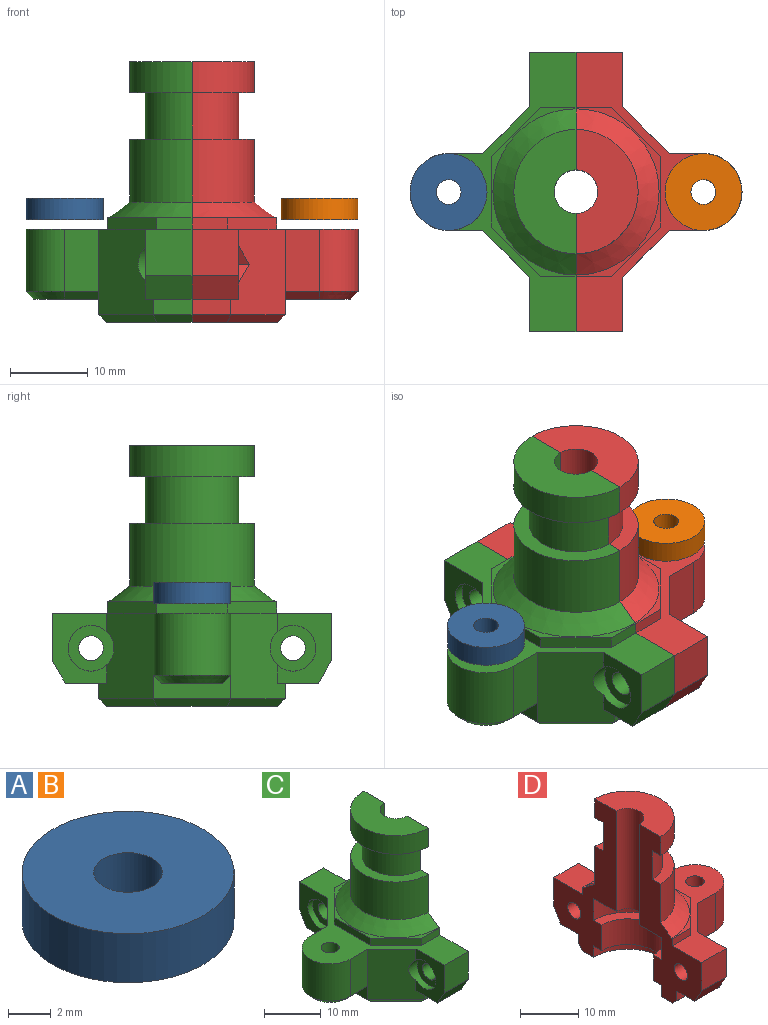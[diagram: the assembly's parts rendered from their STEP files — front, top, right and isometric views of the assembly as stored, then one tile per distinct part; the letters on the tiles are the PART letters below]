
ASSEMBLY  parts=4 mates=1
PART A: 4 faces, bbox 9.9x9.9x2.8 mm
  f0: plane 9.9x9.9mm, normal (0,0,1), area 68.9mm2, adj f2,f3
  f1: plane 9.9x9.9mm, normal (0,0,-1), area 68.9mm2, adj f2,f3
  f2: cylinder r=4.95mm len=9.9mm, axis (0,0,-1), area 87.1mm2, adj f0,f1
  f3: cylinder r=1.6mm len=3.2mm, axis (0,0,-1), area 28.1mm2, adj f0,f1
PART B: same geometry as A
PART C: 58 faces, bbox 21.4x36x33.6 mm
  f0: plane 9x7.03mm, normal (-1,0,0), area 36mm2, adj f12,f13,f15,f19,f32,f49
  f1: plane 6x5.33mm, normal (0,0,-1), area 26.3mm2, adj f16,f20,f36,f37,f40
  f2: cylinder r=8mm len=16mm, axis (0,0,-1), area 203.6mm2, adj f8,f11,f39,f40
  f3: plane 4.52x1.5mm, normal (0,1,0), area 6.8mm2, adj f5,f12,f29,f40
  f4: plane 4.52x1.5mm, normal (0,-1,0), area 6.8mm2, adj f5,f12,f31,f39
  f5: plane 21.8x10.9mm, normal (0,0,1), area 17mm2, adj f3,f4,f11,f29,f30,f31,f39,f40
  f6: cylinder r=6mm len=12mm, axis (0,0,-1), area 113.1mm2, adj f7,f8,f39,f40
  f7: plane 16x8mm, normal (0,0,-1), area 44mm2, adj f6,f10,f39,f40
  f8: plane 16x8mm, normal (0,0,1), area 44mm2, adj f2,f6,f39,f40
  f9: plane 16x8mm, normal (0,0,1), area 88.2mm2, adj f10,f27,f39,f40
  f10: cylinder r=8mm len=16mm, axis (0,0,-1), area 100.5mm2, adj f7,f9,f39,f40
  f11: cone r=8mm half-angle=53.5deg, axis (0,0,-1), area 98.7mm2, adj f2,f5,f39,f40
  f12: plane 36x21.37mm, normal (0,0,1), area 189.3mm2, adj f0,f3,f4,f13,f14,f29,f30,f31
  f13: plane 6x6mm, normal (0,-1,0), area 36mm2, adj f0,f12,f19,f39
  f14: plane 6.06x6mm, normal (0,1,0), area 36.3mm2, adj f12,f20,f37,f40
  f15: plane 6x5.3mm, normal (0,0,-1), area 26.1mm2, adj f0,f18,f19,f32,f39
  f16: plane 4.97x2mm, normal (0,1,0), area 9.9mm2, adj f1,f36,f40,f57
  f17: plane 22x11mm, normal (0,0,-1), area 92.3mm2, adj f21,f39,f40,f53,f54,f55,f56,f57
  f18: plane 4.97x2mm, normal (0,-1,0), area 9.9mm2, adj f15,f32,f39,f53
  f19: plane 6x3mm, normal (0,-0.87,-0.5), area 20.8mm2, adj f0,f13,f15,f39
  f20: plane 6x2.94mm, normal (0,0.87,-0.5), area 20.4mm2, adj f1,f14,f37,f40
  f21: cylinder r=8.3mm len=16.6mm, axis (0,0,-1), area 62.6mm2, adj f17,f25,f39,f40
  f22: plane 16.6x8.3mm, normal (0,0,-1), area 95.9mm2, adj f26,f27,f39,f40
  f23: cylinder r=6.3mm len=12.6mm, axis (0,0,-1), area 106.9mm2, adj f24,f25,f39,f40
  f24: plane 16.6x8.3mm, normal (0,0,1), area 45.9mm2, adj f23,f26,f39,f40
  f25: plane 16.6x8.3mm, normal (0,0,-1), area 45.9mm2, adj f21,f23,f39,f40
  f26: cylinder r=8.3mm len=16.6mm, axis (0,0,-1), area 119.9mm2, adj f22,f24,f39,f40
  f27: cylinder r=2.8mm len=21.2mm, axis (0,0,1), area 186.5mm2, adj f9,f22,f39,f40
  f28: plane 8.37x7.94mm, normal (0,0,-1), area 32.4mm2, adj f38,f43,f50,f51,f52
  f29: plane 6.39x6.39mm, normal (-0.71,0.71,0), area 13.5mm2, adj f3,f5,f12,f30
  f30: plane 9.03x1.5mm, normal (-1,0,0), area 13.5mm2, adj f5,f12,f29,f31
  f31: plane 6.39x6.39mm, normal (-0.71,-0.71,0), area 13.5mm2, adj f4,f5,f12,f30
  f32: plane 11x7.03mm, normal (-0.71,-0.71,0), area 92.4mm2, adj f0,f12,f15,f18,f33,f38,f49,f54
  f33: plane 8x4.4mm, normal (0,-1,0), area 35.2mm2, adj f12,f32,f34,f52
  f34: cylinder r=4.97mm len=9.94mm, axis (0,0,1), area 124.9mm2, adj f12,f33,f35,f51
  f35: plane 8x4.4mm, normal (0,1,0), area 35.2mm2, adj f12,f34,f36,f50
  f36: plane 11x7.03mm, normal (-0.71,0.71,0), area 92.4mm2, adj f1,f12,f16,f35,f37,f38,f46,f56
  f37: plane 9x7.03mm, normal (-1,0,0), area 36.1mm2, adj f1,f12,f14,f20,f36,f46
  f38: plane 9.94x3mm, normal (-1,0,0), area 20.9mm2, adj f28,f32,f36,f50,f52,f55
  f39: plane 33.6x15.2mm, normal (1,0,0), area 203.2mm2, adj f2,f4,f5,f6,f7,f8,f9,f10
  f40: plane 33.6x15.2mm, normal (1,0,0), area 203.3mm2, adj f1,f2,f3,f5,f6,f7,f8,f9
  f41: cylinder r=1.6mm len=7.8mm, axis (0,0,-1), area 78.4mm2, adj f12,f42
  f42: plane 5.9x5.9mm, normal (0,0,-1), area 19.3mm2, adj f41,f43
  f43: cylinder r=2.95mm len=5.9mm, axis (0,0,-1), area 22.2mm2, adj f28,f42
  f44: cylinder r=1.6mm len=4.8mm, axis (-1,0,0), area 48.3mm2, adj f40,f45
  f45: plane 5.9x5.9mm, normal (-1,0,0), area 19.3mm2, adj f44,f46
  f46: cylinder r=2.95mm len=5.9mm, axis (-1,0,0), area 25.2mm2, adj f36,f37,f45
  f47: cylinder r=1.6mm len=4.8mm, axis (-1,0,0), area 48.3mm2, adj f39,f48
  f48: plane 5.9x5.9mm, normal (-1,0,0), area 19.3mm2, adj f47,f49
  f49: cylinder r=2.95mm len=5.9mm, axis (-1,0,0), area 25.2mm2, adj f0,f32,f48
  f50: plane 4.4x1mm, normal (0,0.71,-0.71), area 6.2mm2, adj f28,f35,f38,f51
  f51: cone r=3.97mm half-angle=45deg, axis (0,0,1), area 19.9mm2, adj f28,f34,f50,f52
  f52: plane 4.4x1mm, normal (0,-0.71,-0.71), area 6.2mm2, adj f28,f33,f38,f51
  f53: plane 4.97x1mm, normal (0,-0.71,-0.71), area 6.7mm2, adj f17,f18,f39,f54
  f54: plane 7.44x7.44mm, normal (-0.5,-0.5,-0.71), area 13.5mm2, adj f17,f32,f53,f55
  f55: plane 9.94x1mm, normal (-0.71,0,-0.71), area 13.5mm2, adj f17,f38,f54,f56
  f56: plane 7.44x7.44mm, normal (-0.5,0.5,-0.71), area 13.5mm2, adj f17,f36,f55,f57
  f57: plane 4.97x1mm, normal (0,0.71,-0.71), area 6.7mm2, adj f16,f17,f40,f56
PART D: 68 faces, bbox 21.4x36x33.6 mm
  f0: plane 11x7.03mm, normal (0.71,-0.71,0), area 91.6mm2, adj f1,f10,f11,f27,f30,f32,f48,f49
  f1: plane 9x7.03mm, normal (1,0,0), area 33.8mm2, adj f0,f19,f30,f31,f32,f47,f48,f49
  f2: cylinder r=1.6mm len=4mm, axis (-1,0,0), area 40.2mm2, adj f42,f53
  f3: cylinder r=1.6mm len=4mm, axis (-1,0,0), area 40.2mm2, adj f41,f46
  f4: plane 8.37x7.94mm, normal (0,0,-1), area 32.4mm2, adj f11,f45,f60,f61,f62
  f5: plane 6.39x6.39mm, normal (0.71,-0.71,0), area 13.5mm2, adj f6,f15,f32,f37
  f6: plane 9.03x1.5mm, normal (1,0,0), area 13.5mm2, adj f5,f7,f15,f32
  f7: plane 6.39x6.39mm, normal (0.71,0.71,0), area 13.5mm2, adj f6,f15,f32,f38
  f8: plane 8x4.4mm, normal (0,1,0), area 35.2mm2, adj f9,f12,f32,f60
  f9: cylinder r=4.97mm len=9.94mm, axis (0,0,1), area 124.9mm2, adj f8,f10,f32,f61
  f10: plane 8x4.4mm, normal (0,-1,0), area 35.2mm2, adj f0,f9,f32,f62
  f11: plane 9.94x3mm, normal (1,0,0), area 20.9mm2, adj f0,f4,f12,f60,f62,f65
  f12: plane 11x7.03mm, normal (0.71,0.71,0), area 91.6mm2, adj f8,f11,f13,f29,f32,f40,f54,f59
  f13: plane 9x7.03mm, normal (1,0,0), area 33.9mm2, adj f12,f17,f18,f32,f40,f54,f55,f56
  f14: cone r=8mm half-angle=53.5deg, axis (0,0,-1), area 98.7mm2, adj f15,f39,f41,f42
  f15: plane 21.8x10.9mm, normal (0,0,1), area 17mm2, adj f5,f6,f7,f14,f37,f38,f41,f42
  f16: plane 16x8mm, normal (0,0,1), area 44mm2, adj f36,f39,f41,f42
  f17: plane 6x2.94mm, normal (0,0.87,-0.5), area 20.4mm2, adj f13,f18,f40,f42
  f18: plane 6.06x6mm, normal (0,1,0), area 36.3mm2, adj f13,f17,f32,f42
  f19: plane 6x3mm, normal (0,-0.87,-0.5), area 20.8mm2, adj f1,f30,f31,f41
  f20: cylinder r=2.8mm len=21.2mm, axis (0,0,1), area 186.5mm2, adj f25,f34,f41,f42
  f21: plane 16.6x8.3mm, normal (0,0,-1), area 45.9mm2, adj f24,f26,f41,f42
  f22: cylinder r=8.3mm len=16.6mm, axis (0,0,-1), area 119.9mm2, adj f23,f25,f41,f42
  f23: plane 16.6x8.3mm, normal (0,0,1), area 45.9mm2, adj f22,f24,f41,f42
  f24: cylinder r=6.3mm len=12.6mm, axis (0,0,-1), area 106.9mm2, adj f21,f23,f41,f42
  f25: plane 16.6x8.3mm, normal (0,0,-1), area 95.9mm2, adj f20,f22,f41,f42
  f26: cylinder r=8.3mm len=16.6mm, axis (0,0,-1), area 62.6mm2, adj f21,f28,f41,f42
  f27: plane 4.97x2mm, normal (0,-1,0), area 9.9mm2, adj f0,f30,f41,f63
  f28: plane 22x11mm, normal (0,0,-1), area 92.3mm2, adj f26,f41,f42,f63,f64,f65,f66,f67
  f29: plane 4.97x2mm, normal (0,1,0), area 9.9mm2, adj f12,f40,f42,f67
  f30: plane 6x5.3mm, normal (0,0,-1), area 26.1mm2, adj f0,f1,f19,f27,f41
  f31: plane 6x6mm, normal (0,-1,0), area 36mm2, adj f1,f19,f32,f41
  f32: plane 36x21.37mm, normal (0,0,1), area 189.3mm2, adj f0,f1,f5,f6,f7,f8,f9,f10
  f33: cylinder r=8mm len=16mm, axis (0,0,-1), area 100.5mm2, adj f34,f35,f41,f42
  f34: plane 16x8mm, normal (0,0,1), area 88.2mm2, adj f20,f33,f41,f42
  f35: plane 16x8mm, normal (0,0,-1), area 44mm2, adj f33,f36,f41,f42
  f36: cylinder r=6mm len=12mm, axis (0,0,-1), area 113.1mm2, adj f16,f35,f41,f42
  f37: plane 4.52x1.5mm, normal (0,-1,0), area 6.8mm2, adj f5,f15,f32,f41
  f38: plane 4.52x1.5mm, normal (0,1,0), area 6.8mm2, adj f7,f15,f32,f42
  f39: cylinder r=8mm len=16mm, axis (0,0,-1), area 203.6mm2, adj f14,f16,f41,f42
  f40: plane 6x5.33mm, normal (0,0,-1), area 26.3mm2, adj f12,f13,f17,f29,f42
  f41: plane 33.6x15.2mm, normal (-1,0,0), area 203.2mm2, adj f3,f14,f15,f16,f19,f20,f21,f22
  f42: plane 33.6x15.2mm, normal (-1,0,0), area 203.3mm2, adj f2,f14,f15,f16,f17,f18,f20,f21
  f43: cylinder r=1.6mm len=7.8mm, axis (0,0,-1), area 78.4mm2, adj f32,f44
  f44: plane 5.9x5.9mm, normal (0,0,-1), area 19.3mm2, adj f43,f45
  f45: cylinder r=2.95mm len=5.9mm, axis (0,0,-1), area 22.2mm2, adj f4,f44
  f46: plane 6.81x5.9mm, normal (1,0,0), area 22.1mm2, adj f3,f47,f48,f49,f50,f51,f52
  f47: plane 3.41x2mm, normal (0,0,-1), area 6.8mm2, adj f1,f46,f48,f51
  f48: plane 3.38x2.95mm, normal (0,-0.87,-0.5), area 8.7mm2, adj f0,f1,f46,f47,f49
  f49: plane 3.38x2.95mm, normal (0,-0.87,0.5), area 8.7mm2, adj f0,f1,f46,f48,f50
  f50: plane 3.41x2mm, normal (0,0,1), area 6.8mm2, adj f1,f46,f49,f52
  f51: plane 2.95x2mm, normal (0,0.87,-0.5), area 6.8mm2, adj f1,f46,f47,f52
  f52: plane 2.95x2mm, normal (0,0.87,0.5), area 6.8mm2, adj f1,f46,f50,f51
  f53: plane 6.81x5.9mm, normal (1,0,0), area 22.1mm2, adj f2,f54,f55,f56,f57,f58,f59
  f54: plane 3.38x2.95mm, normal (0,0.87,-0.5), area 8.7mm2, adj f12,f13,f53,f55,f59
  f55: plane 3.41x2mm, normal (0,0,-1), area 6.8mm2, adj f13,f53,f54,f56
  f56: plane 2.95x2mm, normal (0,-0.87,-0.5), area 6.8mm2, adj f13,f53,f55,f57
  f57: plane 2.95x2mm, normal (0,-0.87,0.5), area 6.8mm2, adj f13,f53,f56,f58
  f58: plane 3.41x2mm, normal (0,0,1), area 6.8mm2, adj f13,f53,f57,f59
  f59: plane 3.38x2.95mm, normal (0,0.87,0.5), area 8.7mm2, adj f12,f13,f53,f54,f58
  f60: plane 4.4x1mm, normal (0,0.71,-0.71), area 6.2mm2, adj f4,f8,f11,f61
  f61: cone r=4.97mm half-angle=45deg, axis (0,0,1), area 19.9mm2, adj f4,f9,f60,f62
  f62: plane 4.4x1mm, normal (0,-0.71,-0.71), area 6.2mm2, adj f4,f10,f11,f61
  f63: plane 4.97x1mm, normal (0,-0.71,-0.71), area 6.7mm2, adj f27,f28,f41,f64
  f64: plane 7.44x7.44mm, normal (0.5,-0.5,-0.71), area 13.5mm2, adj f0,f28,f63,f65
  f65: plane 9.94x1mm, normal (0.71,0,-0.71), area 13.5mm2, adj f11,f28,f64,f66
  f66: plane 7.44x7.44mm, normal (0.5,0.5,-0.71), area 13.5mm2, adj f12,f28,f65,f67
  f67: plane 4.97x1mm, normal (0,0.71,-0.71), area 6.7mm2, adj f28,f29,f42,f66
PLACE A rot(axis=(-1,0,0),180deg) t=(0,77.2,-6)mm
PLACE B rot(axis=(-1,0,0),180deg) t=(32.8,77.2,-6)mm
PLACE C t=(0,1.22,0)mm
PLACE D t=(0,1.22,0)mm
MATE fastened C.f47 <-> D.f3  axis (1,0,0) through (-32,26.22,-9.5)mm
